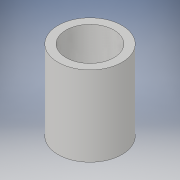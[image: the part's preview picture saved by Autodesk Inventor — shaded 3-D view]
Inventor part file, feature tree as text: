
AUTODESK INVENTOR PART (.ipt)
format: ipt  version: 2019.4 (Build 234330000, 330)  size: 97,280 bytes
history: native  units: mm
features: extrude x1, sketch x1
ambient origin geometry x8: Origin, YZ Plane, XZ Plane, XY Plane, X Axis, Y Axis, Z Axis, Center Point
bodies: Solid1 (feature_tree)
feature tree (2):
  extrude  "Extrusion1"  Depth=5.0mm
  sketch  "Sketch1"  dims[d0=3.0mm d1=4.0mm d2=5.0mm d3=0.0mm]
